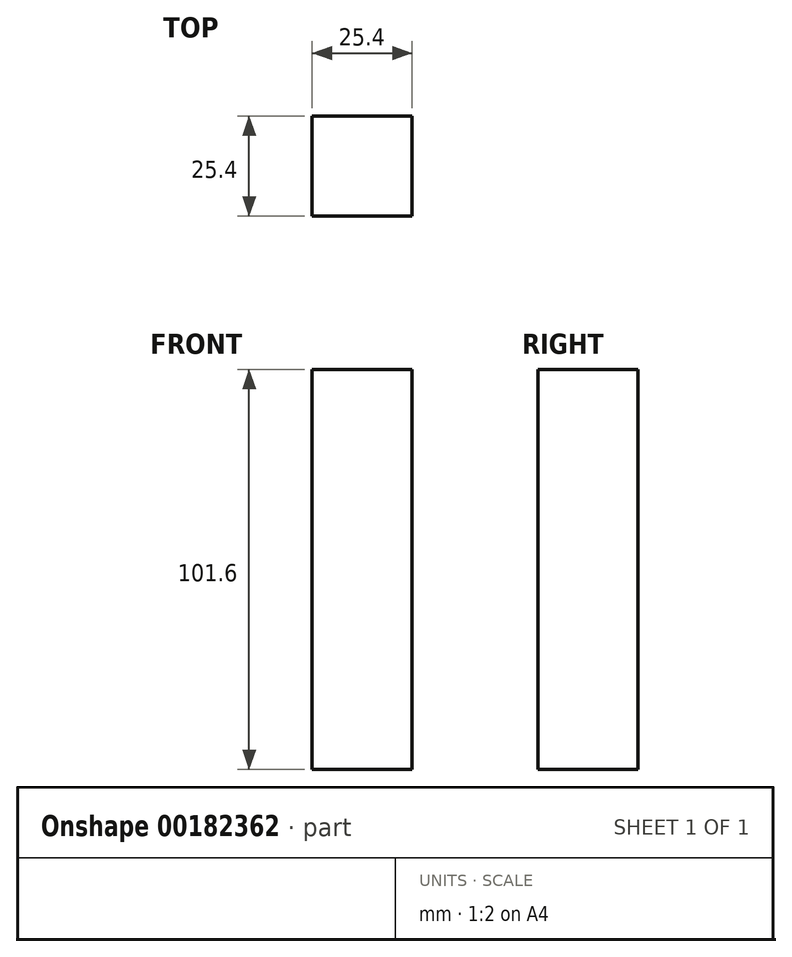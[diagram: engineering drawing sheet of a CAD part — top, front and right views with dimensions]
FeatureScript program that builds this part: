
annotation { "Feature Type Name" : "Feature", "Feature Type Description" : "" }
export const myFeature = defineFeature(function(context is Context, id is Id, definition is map)
    precondition{}
    {
        {
            var Q0;
            Q0=qCreatedBy(makeId("Top.planeOp"),FACE);
            var sketch = newSketch(context, id + "F0", { "sketchPlane" : qUnion([Q0])});
            skLineSegment(sketch, "E0.bottom", {"start": v(0, 0) * mm, "end": v(25.4, 0) * mm});
            skLineSegment(sketch, "E0.top", {"start": v(0, -25.4) * mm, "end": v(25.4, -25.4) * mm});
            skLineSegment(sketch, "E0.left", {"start": v(0, 0) * mm, "end": v(0, -25.4) * mm});
            skLineSegment(sketch, "E0.right", {"start": v(25.4, 0) * mm, "end": v(25.4, -25.4) * mm});
            skSolve(sketch);
        }
        {
            var Q0;
            Q0 = qSketchRegion(id + "F0", true);
            extrude(context, id + "F1", {"entities" : qUnion([Q0]), "depth" : 101.6 * mm});
        }
    });
